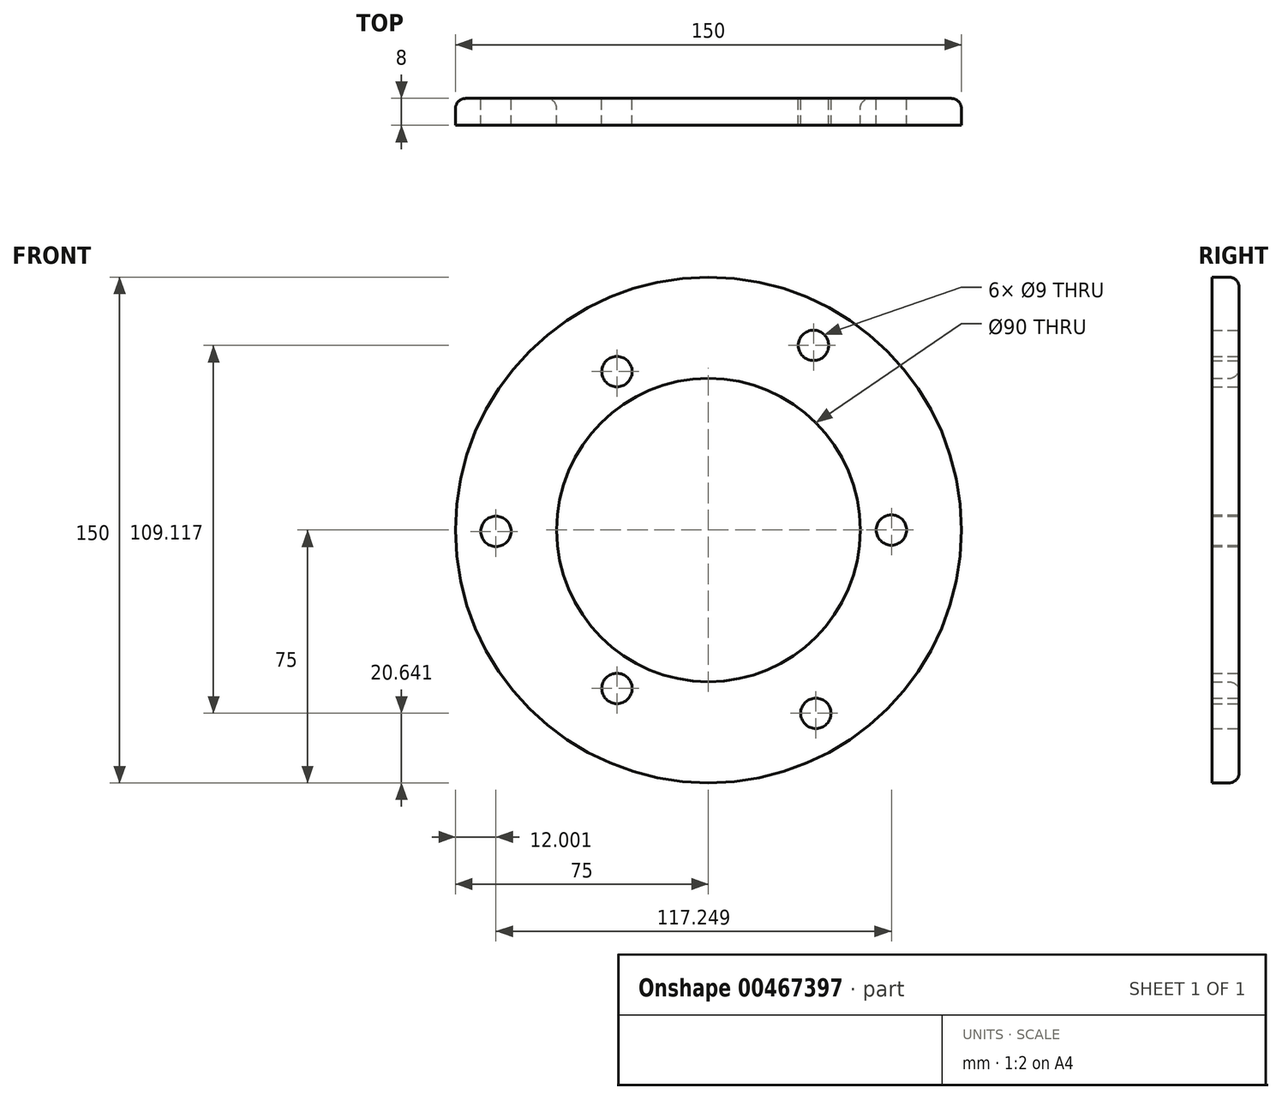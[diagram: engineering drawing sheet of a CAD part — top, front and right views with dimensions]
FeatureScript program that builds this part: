
annotation { "Feature Type Name" : "Feature", "Feature Type Description" : "" }
export const myFeature = defineFeature(function(context is Context, id is Id, definition is map)
    precondition{}
    {
        {
            var Q0;
            Q0=qCreatedBy(makeId("Front.planeOp"),FACE);
            var sketch = newSketch(context, id + "F0", { "sketchPlane" : qUnion([Q0])});
            skCircle(sketch, "E0", {"center": v(0, 0) * mm, "radius": 45 * mm});
            skCircle(sketch, "E1", {"center": v(54.25, 0) * mm, "radius": 4.5 * mm});
            skCircle(sketch, "E2.1.0", {"center": v(-27.12, 46.98) * mm, "radius": 4.5 * mm});
            skCircle(sketch, "E2.2.0", {"center": v(-27.13, -46.98) * mm, "radius": 4.5 * mm});
            skCircle(sketch, "E3", {"center": v(0, 0) * mm, "radius": 75 * mm});
            skCircle(sketch, "E4", {"center": v(31.15, 54.76) * mm, "radius": 4.5 * mm});
            skCircle(sketch, "E5.1.0", {"center": v(31.85, -54.36) * mm, "radius": 4.5 * mm});
            skCircle(sketch, "E5.2.0", {"center": v(-63, -0.4) * mm, "radius": 4.5 * mm});
            skLineSegment(sketch, "E5.anchor1", {"start": v(0, 0) * mm, "end": v(31.15, 54.76) * mm, "construction": true});
            skLineSegment(sketch, "E5.anchor2", {"start": v(0, 0) * mm, "end": v(-63, -0.4) * mm, "construction": true});
            skSolve(sketch);
        }
        {
            var Q0;
            Q0=makeQuery(id+"F0.imprint","IMPRINT",FACE,{"disambiguationData":[TD([[makeQuery(id+"F0.imprint","IMPRINT",EDGE,{"derivedFrom":sQuery(id+"F0.wireOp",EDGE,"E0")}),-1.0]])]});
            extrude(context, id + "F1", {"entities" : qUnion([Q0]), "depth" : 8 * mm, "offsetDistance" : 25 * mm});
        }
        {
            var Q0;
            Q0=makeQuery(id+"F1.opExtrude","CAP_EDGE",EDGE,{"disambiguationData":[OSD([sQuery(id+"F0.wireOp",EDGE,"E0")])],"isStart":true});
            fillet(context, id + "F2", {"entities" : qUnion([Q0]), "tangentPropagation" : true, "radius" : 3 * mm, "defaultsChanged" : true, "vertexSettings" : [], "allowEdgeOverflow" : false});
        }
        {
            var Q0;
            Q0=makeQuery(id+"F1.opExtrude","CAP_EDGE",EDGE,{"disambiguationData":[OSD([sQuery(id+"F0.wireOp",EDGE,"E3")])],"isStart":true});
            fillet(context, id + "F3", {"entities" : qUnion([Q0]), "tangentPropagation" : true, "radius" : 3 * mm, "defaultsChanged" : true, "vertexSettings" : [], "allowEdgeOverflow" : false});
        }
    });
